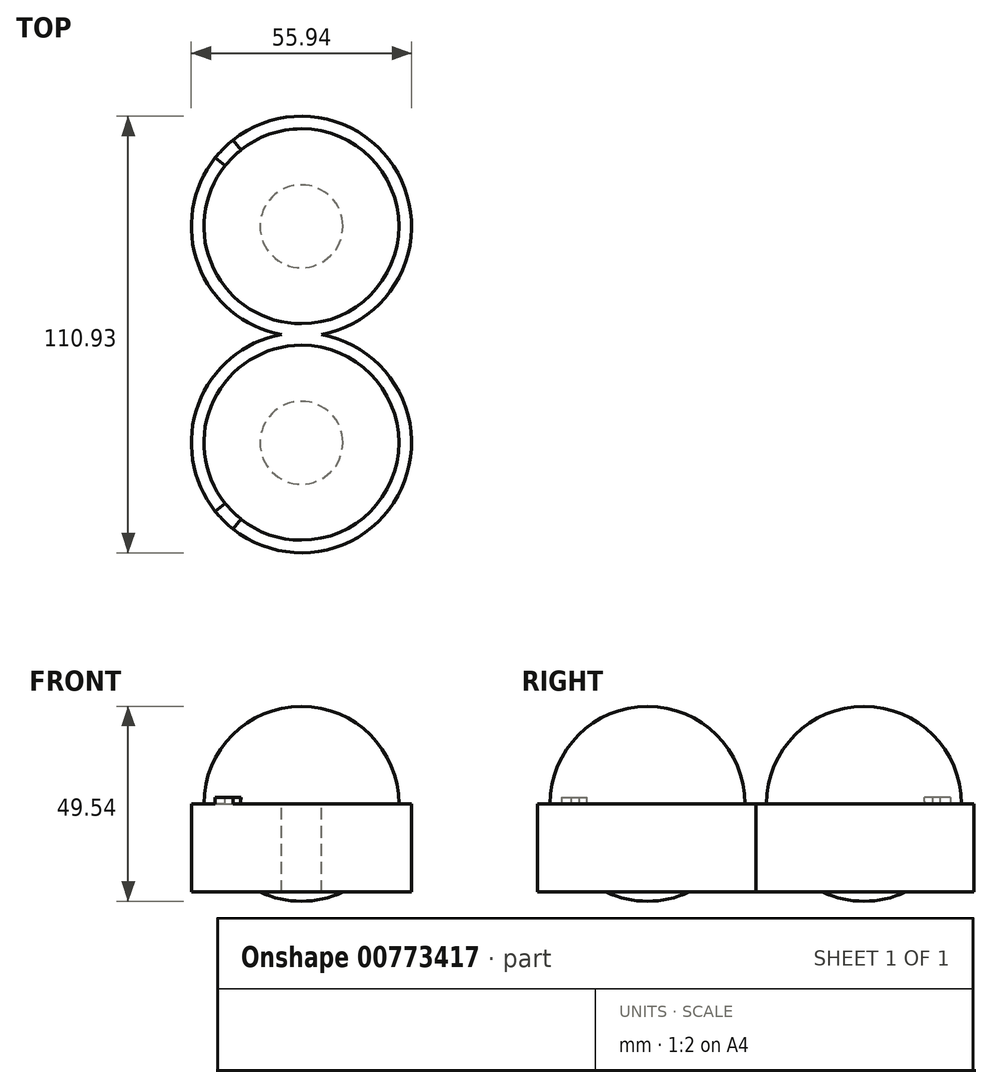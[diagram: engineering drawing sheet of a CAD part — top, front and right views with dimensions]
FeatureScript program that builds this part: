
annotation { "Feature Type Name" : "Feature", "Feature Type Description" : "" }
export const myFeature = defineFeature(function(context is Context, id is Id, definition is map)
    precondition{}
    {
        {
            var Q0;
            Q0=qCreatedBy(makeId("Top.planeOp"),FACE);
            var sketch = newSketch(context, id + "F0", { "sketchPlane" : qUnion([Q0])});
            skLineSegment(sketch, "E0.bottom", {"start": v(-44.45, 44.45) * mm, "end": v(44.45, 44.45) * mm});
            skLineSegment(sketch, "E0.top", {"start": v(-44.45, -44.45) * mm, "end": v(44.45, -44.45) * mm});
            skLineSegment(sketch, "E0.left", {"start": v(-44.45, 44.45) * mm, "end": v(-44.45, -44.45) * mm});
            skLineSegment(sketch, "E0.right", {"start": v(44.45, 44.45) * mm, "end": v(44.45, -44.45) * mm});
            skCircle(sketch, "E1", {"center": v(0, 0) * mm, "radius": 24.77 * mm, "construction": true});
            skLineSegment(sketch, "E2", {"start": v(0, 44.45) * mm, "end": v(0, -44.45) * mm, "construction": true});
            skPoint(sketch, "E3", {"position": v(24.77, 0) * mm});
            skSolve(sketch);
        }
        {
            var Q0;
            Q0=makeQuery(id+"F0.imprint","IMPRINT",FACE,{"disambiguationData":[TD([[makeQuery(id+"F0.imprint","IMPRINT",EDGE,{"derivedFrom":sQuery(id+"F0.wireOp",EDGE,"E0.bottom")}),-1.0]])]});
            extrude(context, id + "F1", {"entities" : qUnion([Q0]), "oppositeDirection" : true, "depth" : 44.83 * mm / 2, "offsetDistance" : 25.4 * mm});
        }
        {
            var Q0;
            Q0=makeQuery(id+"F0.imprint","IMPRINT",FACE,{"disambiguationData":[TD([[makeQuery(id+"F0.imprint","IMPRINT",EDGE,{"derivedFrom":sQuery(id+"F0.wireOp",EDGE,"E0.bottom")}),-1.0]])]});
            var sketch = newSketch(context, id + "F2", { "sketchPlane" : qUnion([Q0])});
            skArc(sketch, "E4", {"start": v(0, 24.77) * mm, "mid": v(-24.77, 0) * mm, "end": v(0, -24.77) * mm});
            skLineSegment(sketch, "E5", {"start": v(0, 24.77) * mm, "end": v(0, -24.77) * mm});
            skSolve(sketch);
        }
        {
            var Q0;
            Q0=makeQuery(id+"F2.imprint","IMPRINT",FACE,{"disambiguationData":[TD([[makeQuery(id+"F2.imprint","IMPRINT",EDGE,{"derivedFrom":sQuery(id+"F2.wireOp",EDGE,"E4")}),1.0]])]});
            var Q1;
            Q1=sQuery(id+"F0.wireOp",EDGE,"E2");
            revolve(context, id + "F3", {"operationType" : NewBodyOperationType.ADD, "surfaceOperationType" : NewSurfaceOperationType.NEW, "entities" : qUnion([Q0]), "axis" : qUnion([Q1]), "revolveType" : RevolveType.FULL});
        }
        {
            var Q0;
            Q0=makeQuery(id+"F0.imprint","IMPRINT",FACE,{"disambiguationData":[TD([[makeQuery(id+"F0.imprint","IMPRINT",EDGE,{"derivedFrom":sQuery(id+"F0.wireOp",EDGE,"E0.bottom")}),-1.0]])]});
            var sketch = newSketch(context, id + "F4", { "sketchPlane" : qUnion([Q0])});
            skCircle(sketch, "E6", {"center": v(0, 0) * mm, "radius": 34.32 * mm});
            skPoint(sketch, "E7", {"position": v(-34.32, 0) * mm});
            skPoint(sketch, "E8", {"position": v(-24.77, 0) * mm});
            skLineSegment(sketch, "E9.0", {"start": v(-44.45, 44.45) * mm, "end": v(44.45, 44.45) * mm});
            skLineSegment(sketch, "E9.1", {"start": v(-44.45, 44.45) * mm, "end": v(-44.45, -44.45) * mm});
            skLineSegment(sketch, "E9.2", {"start": v(-44.45, -44.45) * mm, "end": v(44.45, -44.45) * mm});
            skLineSegment(sketch, "E9.3", {"start": v(44.45, 44.45) * mm, "end": v(44.45, -44.45) * mm});
            skCircle(sketch, "E10", {"center": v(0, 0) * mm, "radius": 27.97 * mm});
            skPoint(sketch, "E11", {"position": v(-27.97, 0) * mm});
            skPoint(sketch, "E11.positionSnap0", {"position": v(-44.45, 0) * mm});
            skSolve(sketch);
        }
        {
            var Q0;
            Q0=makeQuery(id+"F0.imprint","IMPRINT",FACE,{"disambiguationData":[TD([[makeQuery(id+"F0.imprint","IMPRINT",EDGE,{"derivedFrom":sQuery(id+"F0.wireOp",EDGE,"E0.bottom")}),-1.0]])]});
            var sketch = newSketch(context, id + "F5", { "sketchPlane" : qUnion([Q0])});
            skCircle(sketch, "E12.0", {"center": v(0, 0) * mm, "radius": 27.97 * mm});
            skLineSegment(sketch, "E12.1", {"start": v(-44.45, 44.45) * mm, "end": v(44.45, 44.45) * mm});
            skLineSegment(sketch, "E12.2", {"start": v(-44.45, 44.45) * mm, "end": v(-44.45, -44.45) * mm});
            skLineSegment(sketch, "E12.3", {"start": v(44.45, 44.45) * mm, "end": v(44.45, -44.45) * mm});
            skLineSegment(sketch, "E12.4", {"start": v(-44.45, -44.45) * mm, "end": v(44.45, -44.45) * mm});
            skSolve(sketch);
        }
        {
            var Q0;
            Q0=makeQuery(id+"F0.imprint","IMPRINT",FACE,{"disambiguationData":[TD([[makeQuery(id+"F0.imprint","IMPRINT",EDGE,{"derivedFrom":sQuery(id+"F0.wireOp",EDGE,"E0.bottom")}),-1.0]])]});
            var sketch = newSketch(context, id + "F6", { "sketchPlane" : qUnion([Q0])});
            skCircle(sketch, "E13", {"center": v(0, 0) * mm, "radius": 36.86 * mm});
            skLineSegment(sketch, "E14.0", {"start": v(-44.45, 44.45) * mm, "end": v(44.45, 44.45) * mm});
            skLineSegment(sketch, "E14.1", {"start": v(-44.45, 44.45) * mm, "end": v(-44.45, -44.45) * mm});
            skLineSegment(sketch, "E14.2", {"start": v(-44.45, -44.45) * mm, "end": v(44.45, -44.45) * mm});
            skLineSegment(sketch, "E14.3", {"start": v(44.45, 44.45) * mm, "end": v(44.45, -44.45) * mm});
            skPoint(sketch, "E15", {"position": v(-36.86, 0) * mm});
            skSolve(sketch);
        }
        {
            var Q0;
            Q0=qCreatedBy(makeId("Front.planeOp"),FACE);
            var sketch = newSketch(context, id + "F7", { "sketchPlane" : qUnion([Q0])});
            skLineSegment(sketch, "E16", {"start": v(0, 0) * mm, "end": v(0, 22.42) * mm});
            skSolve(sketch);
        }
        {
            var Q0;
            Q0=makeQuery(id+"F0.imprint","IMPRINT",FACE,{"disambiguationData":[TD([[makeQuery(id+"F0.imprint","IMPRINT",EDGE,{"derivedFrom":sQuery(id+"F0.wireOp",EDGE,"E0.bottom")}),-1.0]])]});
            var sketch = newSketch(context, id + "F8", { "sketchPlane" : qUnion([Q0])});
            skArc(sketch, "E17.0", {"start": v(-17.4, 21.9) * mm, "mid": v(-19.77, 19.77) * mm, "end": v(-21.9, 17.4) * mm});
            skLineSegment(sketch, "E18", {"start": v(-11.6, 9.23) * mm, "end": v(-9.23, 11.6) * mm});
            skLineSegment(sketch, "E19", {"start": v(-10.42, 10.42) * mm, "end": v(0, 0) * mm, "construction": true});
            skLineSegment(sketch, "E20", {"start": v(-10.42, 10.42) * mm, "end": v(-44.45, 44.45) * mm, "construction": true});
            skLineSegment(sketch, "E21", {"start": v(-21.9, 17.4) * mm, "end": v(-11.6, 9.23) * mm});
            skLineSegment(sketch, "E22", {"start": v(-17.4, 21.9) * mm, "end": v(-9.23, 11.6) * mm});
            skSolve(sketch);
        }
        {
            var Q0;
            Q0=qSketchRegion(id+"F5",true);
            extrude(context, id + "F9", {"entities" : qUnion([Q0]), "operationType" : NewBodyOperationType.ADD, "depth" : 19.05 * mm, "offsetDistance" : 25.4 * mm});
        }
        {
            var Q0;
            Q0=qSketchRegion(id+"F6",true);
            var Q1;
            Q1=sQuery(id+"F7.wireOp",VERTEX,"E16.end");
            extrude(context, id + "F10", {"entities" : qUnion([Q0]), "operationType" : NewBodyOperationType.ADD, "depth" : 38.1 * mm, "endBoundEntityVertex" : qUnion([Q1]), "offsetDistance" : 25.4 * mm});
        }
        {
            var Q0;
            Q0=qSketchRegion(id+"F8",true);
            extrude(context, id + "F11", {"entities" : qUnion([Q0]), "operationType" : NewBodyOperationType.ADD, "depth" : 1.59 * mm, "offsetDistance" : 25.4 * mm});
        }
        {
            var Q0;
            Q0=makeQuery(id+"F1.opExtrude","CAP_FACE",FACE,{"disambiguationData":[OSD([sQuery(id+"F0.wireOp",EDGE,"E0.bottom"),sQuery(id+"F0.wireOp",EDGE,"E0.top"),sQuery(id+"F0.wireOp",EDGE,"E0.left"),sQuery(id+"F0.wireOp",EDGE,"E0.right")])],"isStart":false});
            var sketch = newSketch(context, id + "F12", { "sketchPlane" : qUnion([Q0])});
            skLineSegment(sketch, "E23.bottom", {"start": v(44.45, 27.5) * mm, "end": v(-60.76, 27.5) * mm});
            skLineSegment(sketch, "E23.top", {"start": v(44.45, 44.45) * mm, "end": v(-60.76, 44.45) * mm});
            skLineSegment(sketch, "E23.left", {"start": v(44.45, 44.45) * mm, "end": v(44.45, 27.5) * mm});
            skLineSegment(sketch, "E23.right", {"start": v(-60.76, 44.45) * mm, "end": v(-60.76, 27.5) * mm});
            skSolve(sketch);
        }
        {
            var Q0;
            Q0 = qSketchRegion(id + "F12", true);
            extrude(context, id + "F13", {"entities" : qUnion([Q0]), "operationType" : NewBodyOperationType.REMOVE, "endBound" : BoundingType.THROUGH_ALL, "oppositeDirection" : true, "depth" : 25.4 * mm, "offsetDistance" : 25.4 * mm});
        }
        {
            var Q0;
            Q0=makeQuery(id+"F1.opExtrude","SWEPT_BODY",BODY,{"disambiguationData":[OSD([sQuery(id+"F0.wireOp",EDGE,"E0.bottom"),sQuery(id+"F0.wireOp",EDGE,"E0.top"),sQuery(id+"F0.wireOp",EDGE,"E0.left"),sQuery(id+"F0.wireOp",EDGE,"E0.right")])]});
            var Q1;
            Q1=makeQuery(id+"F13.boolean.opBoolean","COPY",FACE,{"derivedFrom":makeQuery(id+"F13.opExtrude","SWEPT_FACE",FACE,{"disambiguationData":[OSD([sQuery(id+"F12.wireOp",EDGE,"E23.bottom")])]})});
            mirror(context, id + "F14", {"operationType" : NewBodyOperationType.ADD, "entities" : qUnion([Q0]), "mirrorPlane" : qUnion([Q1])});
        }
        {
            var Q0;
            Q0=qCreatedBy(makeId("Top.planeOp"),FACE);
            var sketch = newSketch(context, id + "F15", { "sketchPlane" : qUnion([Q0])});
            skLineSegment(sketch, "E24.0", {"start": v(-44.45, -44.45) * mm, "end": v(-44.45, -44.45) * mm});
            skLineSegment(sketch, "E24.1", {"start": v(-44.45, 44.45) * mm, "end": v(-44.45, -44.45) * mm});
            skLineSegment(sketch, "E24.2", {"start": v(-44.45, 44.45) * mm, "end": v(-44.45, 44.45) * mm});
            skLineSegment(sketch, "E24.3", {"start": v(-44.45, -44.45) * mm, "end": v(-44.45, 44.45) * mm});
            skSolve(sketch);
        }
        {
            var Q0;
            {var subQ0=makeQuery(id+"F10.opExtrude","CAP_FACE",FACE,{"disambiguationData":[OSD([sQuery(id+"F6.wireOp",EDGE,"E13"),sQuery(id+"F6.wireOp",EDGE,"E14.0"),sQuery(id+"F6.wireOp",EDGE,"E14.1"),sQuery(id+"F6.wireOp",EDGE,"E14.2"),sQuery(id+"F6.wireOp",EDGE,"E14.3")])],"isStart":false});Q0=makeQuery(id+"F14.boolean.opBoolean","MERGE",FACE,{"derivedFrom":[subQ0,makeQuery(id+"F14.opPattern","COPY",FACE,{"derivedFrom":subQ0,"instanceName":"1"})]});}
            var sketch = newSketch(context, id + "F16", { "sketchPlane" : qUnion([Q0])});
            skPoint(sketch, "E25.center.orphan", {"position": v(0, -55) * mm});
            skArc(sketch, "E26.0", {"start": v(5.1, -27.5) * mm, "mid": v(0, -82.96) * mm, "end": v(-5.1, -27.5) * mm});
            skArc(sketch, "E26.1", {"start": v(5.1, -27.5) * mm, "mid": v(0, 27.97) * mm, "end": v(-5.1, -27.5) * mm});
            skLineSegment(sketch, "E27.bottom", {"start": v(44.45, 44.45) * mm, "end": v(-44.45, 44.45) * mm});
            skLineSegment(sketch, "E27.top", {"start": v(44.45, -99.44) * mm, "end": v(-44.45, -99.44) * mm});
            skLineSegment(sketch, "E27.left", {"start": v(44.45, 44.45) * mm, "end": v(44.45, -99.44) * mm});
            skLineSegment(sketch, "E27.right", {"start": v(-44.45, 44.45) * mm, "end": v(-44.45, -99.44) * mm});
            skSolve(sketch);
        }
        {
            var Q0;
            Q0 = qSketchRegion(id + "F16", true);
            extrude(context, id + "F17", {"entities" : qUnion([Q0]), "operationType" : NewBodyOperationType.REMOVE, "endBound" : BoundingType.THROUGH_ALL, "oppositeDirection" : true, "depth" : 25.4 * mm, "offsetDistance" : 25.4 * mm});
        }
    });
